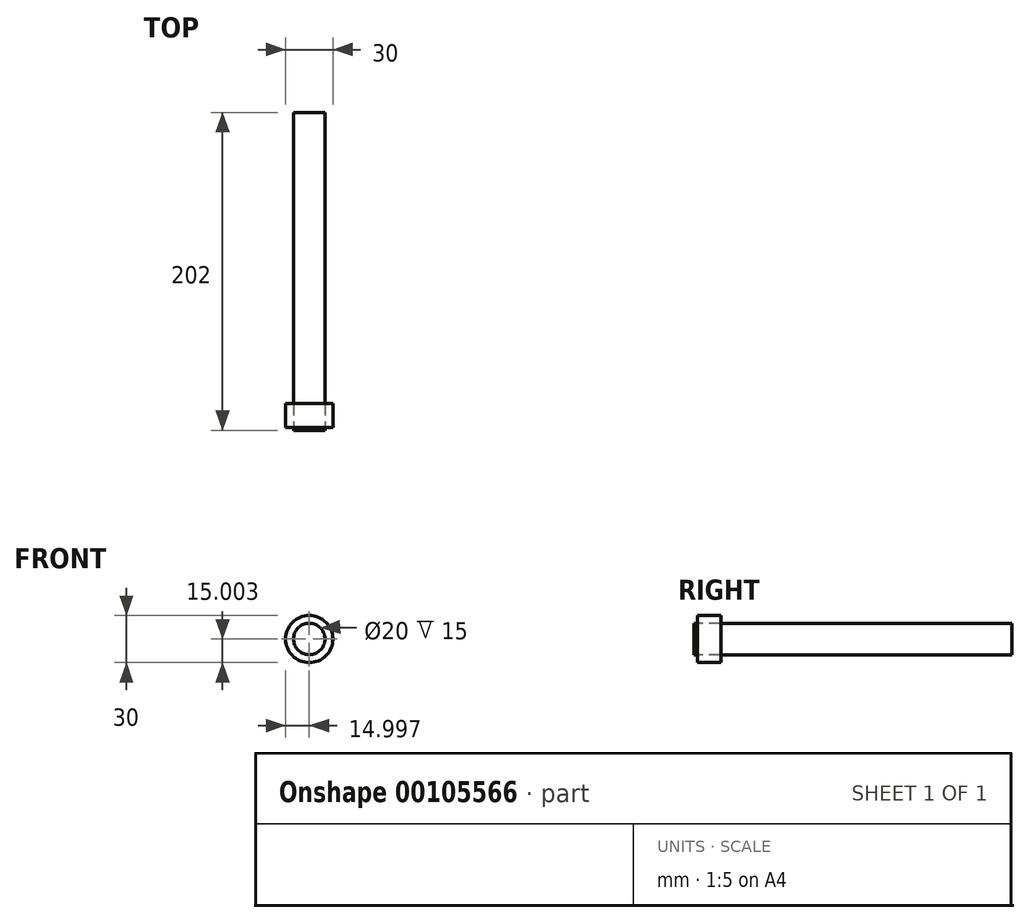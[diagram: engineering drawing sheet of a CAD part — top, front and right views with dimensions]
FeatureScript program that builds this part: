
annotation { "Feature Type Name" : "Feature", "Feature Type Description" : "" }
export const myFeature = defineFeature(function(context is Context, id is Id, definition is map)
    precondition{}
    {
        {
            var Q0;
            Q0=qCreatedBy(makeId("Front.planeOp"),FACE);
            var sketch = newSketch(context, id + "F0", { "sketchPlane" : qUnion([Q0])});
            skCircle(sketch, "E0", {"center": v(-24.82, 23.14) * mm, "radius": 10 * mm});
            skCircle(sketch, "E1", {"center": v(-24.82, 23.14) * mm, "radius": 15 * mm});
            skSolve(sketch);
        }
        {
            var Q0;
            Q0=makeQuery(id+"F0.imprint","IMPRINT",FACE,{"disambiguationData":[TD([[makeQuery(id+"F0.imprint","IMPRINT",EDGE,{"derivedFrom":sQuery(id+"F0.wireOp",EDGE,"E0")}),1.0]])]});
            extrude(context, id + "F1", {"entities" : qUnion([Q0]), "depth" : 2 * mm});
        }
        {
            var Q0;
            Q0=makeQuery(id+"F0.imprint","IMPRINT",FACE,{"disambiguationData":[TD([[makeQuery(id+"F0.imprint","IMPRINT",EDGE,{"derivedFrom":sQuery(id+"F0.wireOp",EDGE,"E0")}),-1.0]])]});
            extrude(context, id + "F2", {"entities" : qUnion([Q0]), "oppositeDirection" : true, "depth" : 15 * mm});
        }
        {
            var Q0;
            Q0=makeQuery(id+"F0.imprint","IMPRINT",FACE,{"disambiguationData":[TD([[makeQuery(id+"F0.imprint","IMPRINT",EDGE,{"derivedFrom":sQuery(id+"F0.wireOp",EDGE,"E0")}),1.0]])]});
            extrude(context, id + "F3", {"entities" : qUnion([Q0]), "oppositeDirection" : true, "depth" : 200 * mm});
        }
    });
